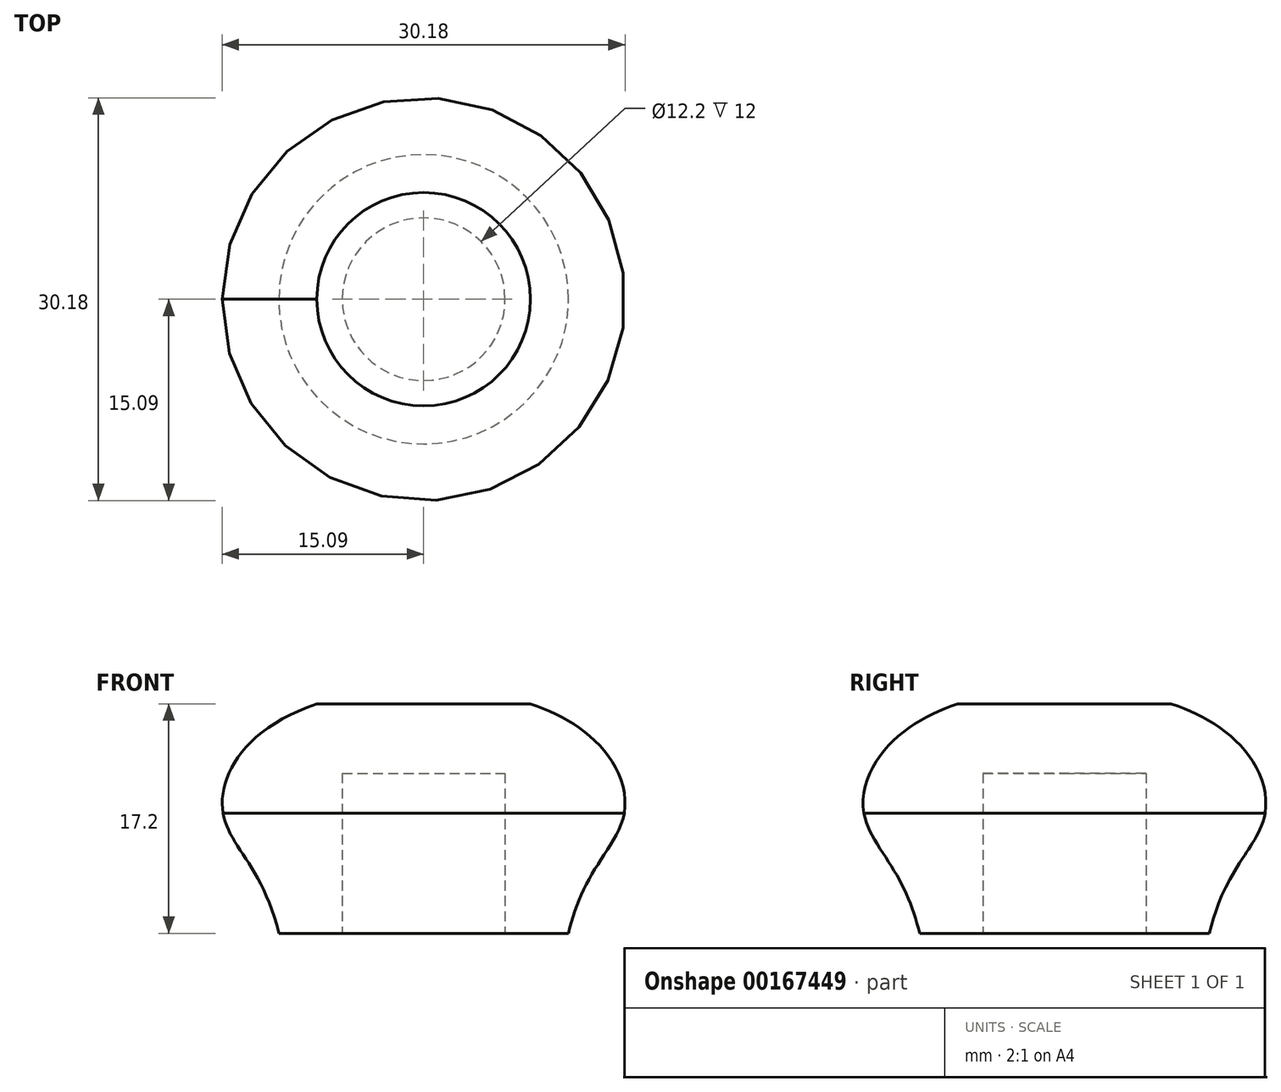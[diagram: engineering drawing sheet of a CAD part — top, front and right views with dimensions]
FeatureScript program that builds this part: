
annotation { "Feature Type Name" : "Feature", "Feature Type Description" : "" }
export const myFeature = defineFeature(function(context is Context, id is Id, definition is map)
    precondition{}
    {
        {
            var Q0;
            Q0=qCreatedBy(makeId("Front.planeOp"),FACE);
            var sketch = newSketch(context, id + "F0", { "sketchPlane" : qUnion([Q0])});
            skLineSegment(sketch, "E0", {"start": v(0, 0) * mm, "end": v(0, 9) * mm});
            skLineSegment(sketch, "E1", {"start": v(0, 9) * mm, "end": v(15.03, 9) * mm});
            skLineSegment(sketch, "E2", {"start": v(0, 0) * mm, "end": v(10.85, 0) * mm});
            skLineSegment(sketch, "E3", {"start": v(0, 0) * mm, "end": v(0, 17.2) * mm});
            skLineSegment(sketch, "E4", {"start": v(0, 17.2) * mm, "end": v(8, 17.2) * mm});
            skFitSpline(sketch, "E5", {"points": [v(10.85, 0) * mm, v(15.03, 9) * mm, v(8, 17.2) * mm], "startDerivative": vector(7.16, 30.4) * mm, "endDerivative": vector(-32.83, 11) * mm});
            skSolve(sketch);
        }
        {
            var Q0;
            Q0 = qSketchRegion(id + "F0", true);
            var Q1;
            Q1=sQuery(id+"F0.wireOp",EDGE,"E3");
            revolve(context, id + "F1", {"entities" : qUnion([Q0]), "axis" : qUnion([Q1]), "revolveType" : RevolveType.FULL});
        }
        {
            var Q0;
            Q0=makeQuery(id+"F1.opRevolve","SWEPT_FACE",FACE,{"disambiguationData":[OSD([sQuery(id+"F0.wireOp",EDGE,"E2")])]});
            var sketch = newSketch(context, id + "F2", { "sketchPlane" : qUnion([Q0])});
            skCircle(sketch, "E6", {"center": v(0, 0) * mm, "radius": 6.1 * mm});
            skSolve(sketch);
        }
        {
            var Q0;
            Q0 = qSketchRegion(id + "F2", true);
            extrude(context, id + "F3", {"entities" : qUnion([Q0]), "operationType" : NewBodyOperationType.REMOVE, "oppositeDirection" : true, "depth" : 12 * mm});
        }
    });
